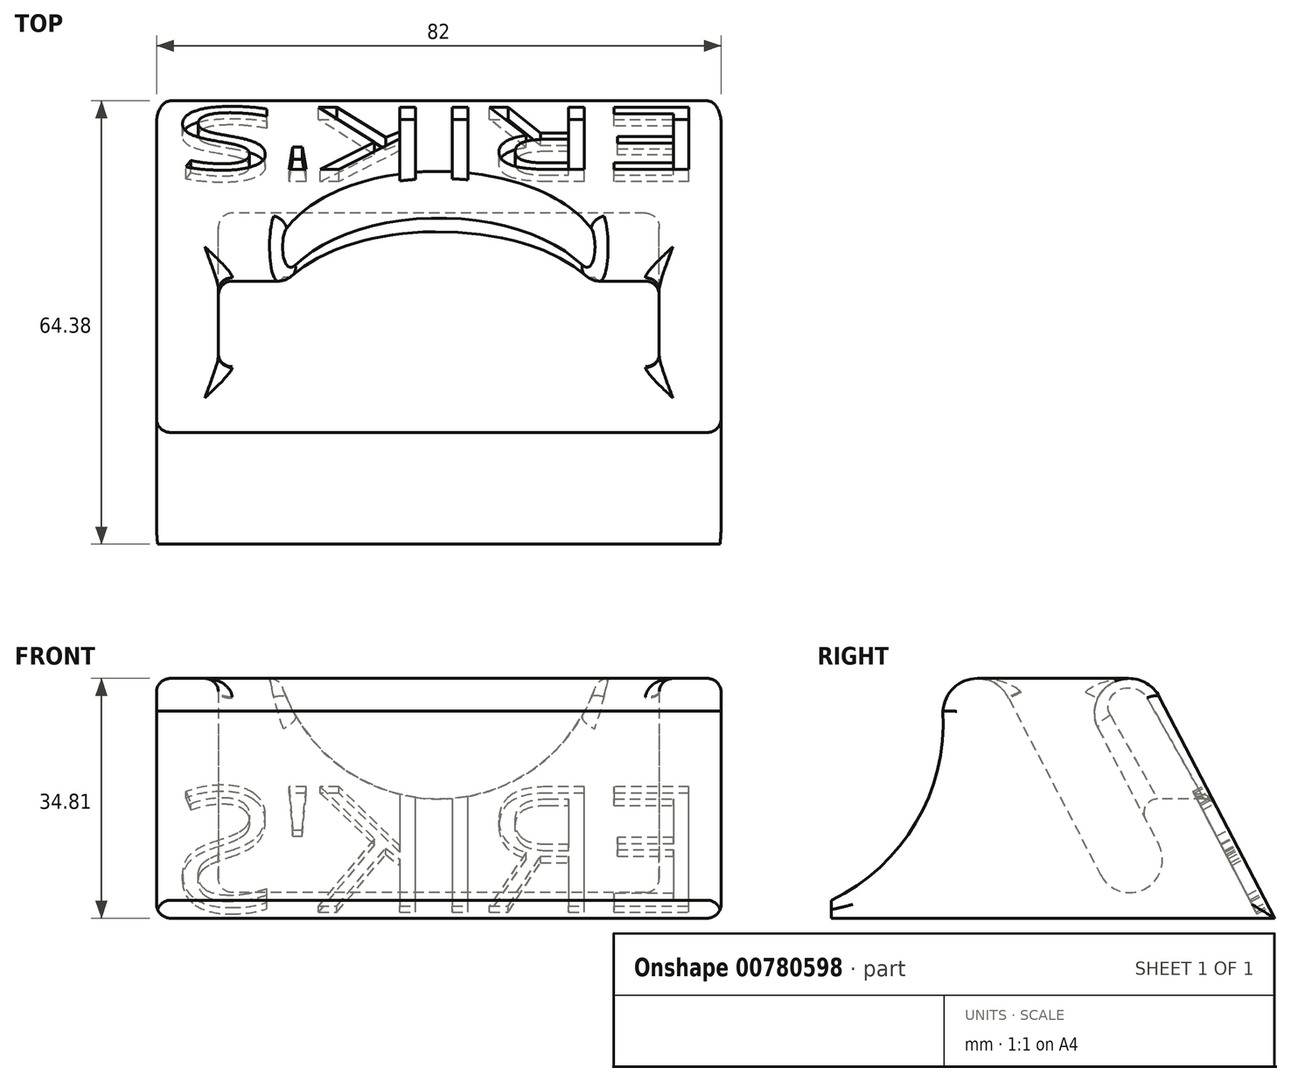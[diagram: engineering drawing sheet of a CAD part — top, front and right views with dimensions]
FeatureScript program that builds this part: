
annotation { "Feature Type Name" : "Feature", "Feature Type Description" : "" }
export const myFeature = defineFeature(function(context is Context, id is Id, definition is map)
    precondition{}
    {
        {
            var Q0;
            Q0=qCreatedBy(makeId("Right.planeOp"),FACE);
            var sketch = newSketch(context, id + "F0", { "sketchPlane" : qUnion([Q0])});
            skLineSegment(sketch, "E0", {"start": v(-19.31, 0) * mm, "end": v(45.07, 0) * mm});
            skLineSegment(sketch, "E1", {"start": v(19.47, 27.5) * mm, "end": v(28.24, 10.66) * mm});
            skArc(sketch, "E2", {"start": v(19.82, 6.27) * mm, "mid": v(26.22, 4.26) * mm, "end": v(28.24, 10.66) * mm});
            skLineSegment(sketch, "E3.0", {"start": v(6.35, 32.12) * mm, "end": v(19.82, 6.27) * mm});
            skPoint(sketch, "E4.orphan", {"position": v(19.82, 6.27) * mm});
            skArc(sketch, "E5", {"start": v(6.35, 32.12) * mm, "mid": v(0.41, 34.58) * mm, "end": v(-3.05, 29.17) * mm});
            skPoint(sketch, "E6.orphan", {"position": v(-1.88, 0) * mm});
            skLineSegment(sketch, "E7.0", {"start": v(28.34, 32.12) * mm, "end": v(45.07, 0) * mm});
            skArc(sketch, "E8", {"start": v(28.34, 32.12) * mm, "mid": v(21.6, 34.24) * mm, "end": v(19.47, 27.5) * mm});
            skArc(sketch, "E9", {"start": v(-19.31, 2.6) * mm, "mid": v(-7.02, 13.85) * mm, "end": v(-3.08, 30.05) * mm});
            skPoint(sketch, "E10.end.orphan", {"position": v(-10.59, 0) * mm});
            skLineSegment(sketch, "E11", {"start": v(-19.31, 0) * mm, "end": v(-19.31, 2.6) * mm});
            skLineSegment(sketch, "E12.0", {"start": v(23.9, 34.81) * mm, "end": v(1.91, 34.81) * mm});
            skSolve(sketch);
        }
        {
            var Q0;
            Q0=qCreatedBy(makeId("Front.planeOp"),FACE);
            var sketch = newSketch(context, id + "F1", { "sketchPlane" : qUnion([Q0])});
            skLineSegment(sketch, "E13", {"start": v(0, 0) * mm, "end": v(0, 41.3) * mm});
            skLineSegment(sketch, "E14", {"start": v(0, 41.3) * mm, "end": v(41, 41.3) * mm});
            skCircle(sketch, "E15", {"center": v(41, 41.3) * mm, "radius": 24 * mm});
            skSolve(sketch);
        }
        {
            var Q0;
            Q0=makeQuery(id+"F0.imprint","IMPRINT",FACE,{"disambiguationData":[TD([[makeQuery(id+"F0.imprint","IMPRINT",EDGE,{"derivedFrom":sQuery(id+"F0.wireOp",EDGE,"E0")}),1.0]])]});
            extrude(context, id + "F2", {"entities" : qUnion([Q0]), "depth" : 82 * mm, "offsetDistance" : 25 * mm});
        }
        {
            var Q0;
            Q0 = qSketchRegion(id + "F1", true);
            extrude(context, id + "F3", {"entities" : qUnion([Q0]), "operationType" : NewBodyOperationType.REMOVE, "oppositeDirection" : true, "depth" : 60 * mm, "offsetDistance" : 25 * mm, "hasSecondDirection" : true, "secondDirectionOppositeDirection" : true, "secondDirectionDepth" : 16 * mm});
        }
        {
            var Q0;
            {var subQ3=sQuery(id+"F0.wireOp",EDGE,"E1");Q0=makeQuery(id+"F0.imprint","IMPRINT",FACE,{"disambiguationData":[TD([[makeQuery(id+"F0.imprint","IMPRINT",EDGE,{"derivedFrom":subQ3}),-1.0]])]});}
            extrude(context, id + "F4", {"entities" : qUnion([Q0]), "operationType" : NewBodyOperationType.ADD, "depth" : 9 * mm, "offsetDistance" : 25 * mm});
        }
        {
            var Q0;
            {var subQ3=sQuery(id+"F0.wireOp",EDGE,"E1");Q0=makeQuery(id+"F0.imprint","IMPRINT",FACE,{"disambiguationData":[TD([[makeQuery(id+"F0.imprint","IMPRINT",EDGE,{"derivedFrom":subQ3}),-1.0]])]});}
            extrude(context, id + "F5", {"entities" : qUnion([Q0]), "operationType" : NewBodyOperationType.ADD, "depth" : 82 * mm, "offsetDistance" : 25 * mm, "hasSecondDirection" : true, "secondDirectionOppositeDirection" : false, "secondDirectionDepth" : 73 * mm});
        }
        {
            var Q0;
            Q0=makeQuery(id+"F4.opExtrude","CAP_EDGE",EDGE,{"disambiguationData":[OSD([sQuery(id+"F0.wireOp",EDGE,"E12.0")])],"isStart":true});
            var Q1;
            {var subQ0=sQuery(id+"F0.wireOp",EDGE,"E8");var subQ1=sQuery(id+"F0.wireOp",EDGE,"E5");var subQ2=sQuery(id+"F0.wireOp",EDGE,"E3.0");var subQ3=sQuery(id+"F0.wireOp",EDGE,"E2");var subQ4=sQuery(id+"F0.wireOp",EDGE,"E1");Q1=makeQuery(id+"F4.boolean.opBoolean","MERGE",FACE,{"derivedFrom":[makeQuery(id+"F2.opExtrude","CAP_FACE",FACE,{"disambiguationData":[OSD([sQuery(id+"F0.wireOp",EDGE,"E0"),subQ4,subQ3,subQ2,subQ1,sQuery(id+"F0.wireOp",EDGE,"E7.0"),subQ0,sQuery(id+"F0.wireOp",EDGE,"E9"),sQuery(id+"F0.wireOp",EDGE,"E11")])],"isStart":true}),makeQuery(id+"F4.opExtrude","CAP_FACE",FACE,{"disambiguationData":[OSD([subQ4,subQ3,subQ2,subQ1,subQ0,sQuery(id+"F0.wireOp",EDGE,"E12.0")])],"isStart":true})]});}
            var Q2;
            {var subQ0=sQuery(id+"F0.wireOp",EDGE,"E8");var subQ1=sQuery(id+"F0.wireOp",EDGE,"E5");var subQ2=sQuery(id+"F0.wireOp",EDGE,"E3.0");var subQ3=sQuery(id+"F0.wireOp",EDGE,"E2");var subQ4=sQuery(id+"F0.wireOp",EDGE,"E1");Q2=makeQuery(id+"F5.boolean.opBoolean","MERGE",FACE,{"derivedFrom":[makeQuery(id+"F2.opExtrude","CAP_FACE",FACE,{"disambiguationData":[OSD([sQuery(id+"F0.wireOp",EDGE,"E0"),subQ4,subQ3,subQ2,subQ1,sQuery(id+"F0.wireOp",EDGE,"E7.0"),subQ0,sQuery(id+"F0.wireOp",EDGE,"E9"),sQuery(id+"F0.wireOp",EDGE,"E11")])],"isStart":false}),makeQuery(id+"F5.opExtrude","CAP_FACE",FACE,{"disambiguationData":[OSD([subQ4,subQ3,subQ2,subQ1,subQ0,sQuery(id+"F0.wireOp",EDGE,"E12.0")])],"isStart":false})]});}
            var Q3;
            Q3=makeQuery(id+"F3.boolean.opBoolean","COPY",FACE,{"derivedFrom":makeQuery(id+"F3.opExtrude","SWEPT_FACE",FACE,{"disambiguationData":[OSD([sQuery(id+"F1.wireOp",EDGE,"E15")])]})});
            fillet(context, id + "F6", {"entities" : qUnion([Q0, Q1, Q2, Q3]), "radius" : 2 * mm, "allowEdgeOverflow" : false});
        }
        {
            var Q0;
            Q0=makeQuery(id+"F4.opExtrude","SWEPT_FACE",FACE,{"disambiguationData":[OSD([sQuery(id+"F0.wireOp",EDGE,"E12.0")])]});
            var Q1;
            Q1=makeQuery(id+"F5.opExtrude","SWEPT_FACE",FACE,{"disambiguationData":[OSD([sQuery(id+"F0.wireOp",EDGE,"E12.0")])]});
            fillet(context, id + "F7", {"entities" : qUnion([Q0, Q1]), "radius" : 2 * mm, "allowEdgeOverflow" : false});
        }
        {
            var Q0;
            Q0=makeQuery(id+"F2.opExtrude","SWEPT_FACE",FACE,{"disambiguationData":[OSD([sQuery(id+"F0.wireOp",EDGE,"E3.0")])]});
            fillet(context, id + "F8", {"entities" : qUnion([Q0]), "radius" : 2 * mm, "tangentPropagation" : true, "allowEdgeOverflow" : false});
        }
        {
            var Q0;
            Q0=makeQuery(id+"F2.opExtrude","SWEPT_FACE",FACE,{"disambiguationData":[OSD([sQuery(id+"F0.wireOp",EDGE,"E7.0")])]});
            cPlane(context, id + "F9", {"entities" : qUnion([Q0]), "cplaneType" : CPlaneType.OFFSET, "offset" : 5 * mm, "width" : 150 * mm, "height" : 150 * mm});
        }
        {
            var Q0;
            Q0=qCreatedBy(id+"F9.planeOp",FACE);
            var sketch = newSketch(context, id + "F10", { "sketchPlane" : qUnion([Q0])});
            skText(sketch, "E16", { "text": "ERIK\'S", "fontName": "OpenSans-Regular.ttf"});
            const initialGuessF10  = {"E16": [-0.08, -0.01883, 1, 0, 0.01968]};
            skSetInitialGuess(sketch, initialGuessF10);
            skSolve(sketch);
        }
        {
            var Q0;
            Q0 = qSketchRegion(id + "F10", true);
            extrude(context, id + "F11", {"entities" : qUnion([Q0]), "operationType" : NewBodyOperationType.REMOVE, "oppositeDirection" : true, "depth" : 7 * mm, "offsetDistance" : 25 * mm});
        }
    });
